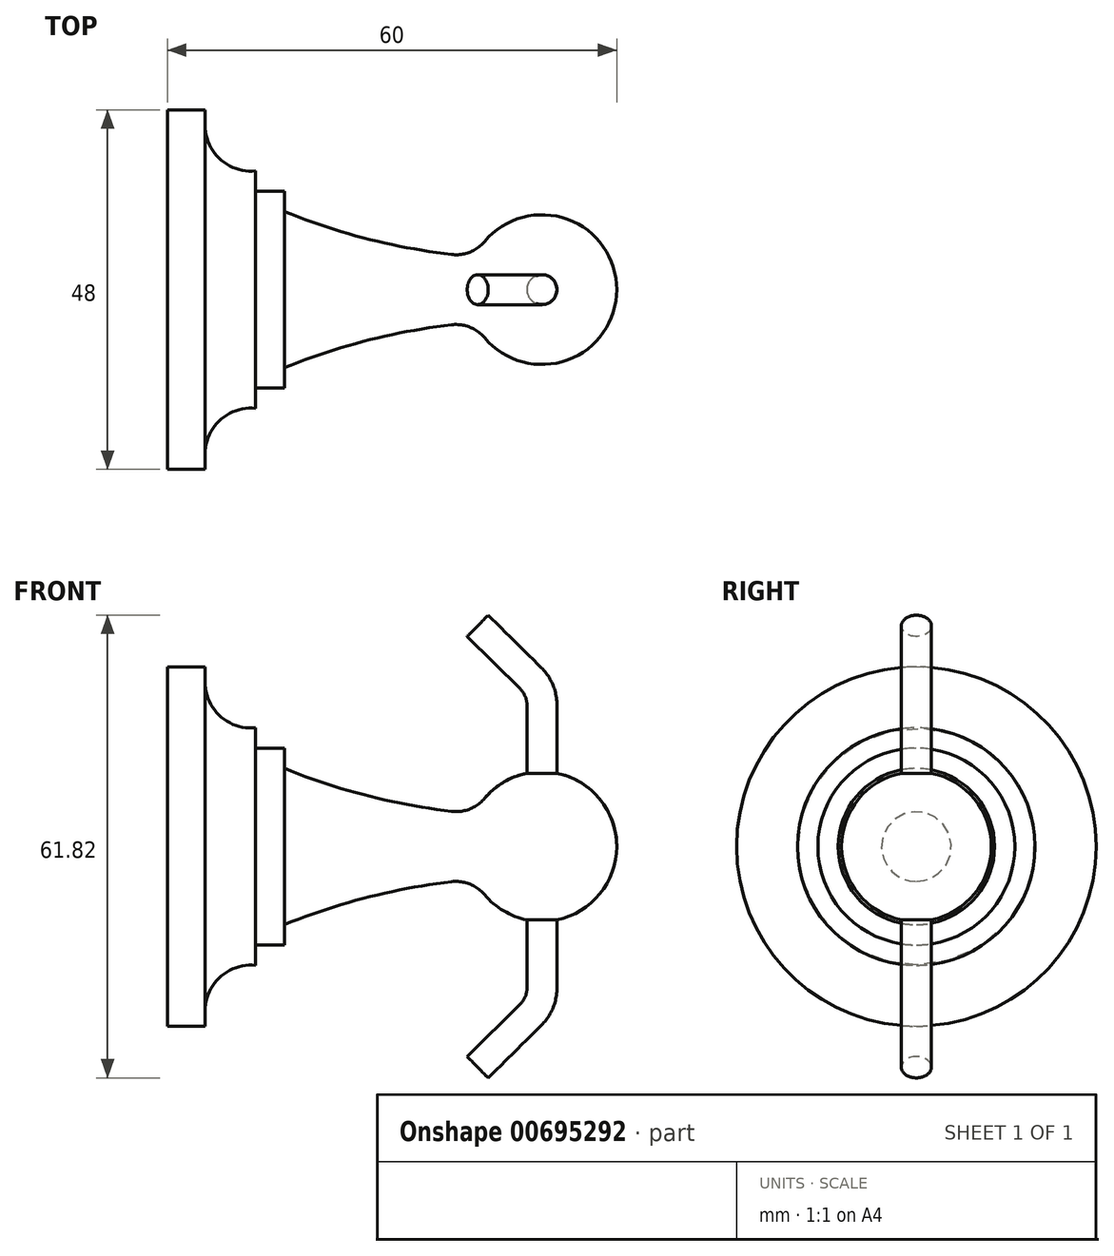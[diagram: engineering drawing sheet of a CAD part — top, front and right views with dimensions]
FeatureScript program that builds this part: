
annotation { "Feature Type Name" : "Feature", "Feature Type Description" : "" }
export const myFeature = defineFeature(function(context is Context, id is Id, definition is map)
    precondition{}
    {
        {
            var Q0;
            Q0=qCreatedBy(makeId("Front.planeOp"),FACE);
            var sketch = newSketch(context, id + "F0", { "sketchPlane" : qUnion([Q0])});
            skLineSegment(sketch, "E0", {"start": v(0, 0) * mm, "end": v(-60, 0) * mm});
            skArc(sketch, "E1", {"start": v(0, 0) * mm, "mid": v(-7.75, 9.74) * mm, "end": v(-18.99, 4.38) * mm});
            skLineSegment(sketch, "E2", {"start": v(-60, 0) * mm, "end": v(-60, 24) * mm});
            skLineSegment(sketch, "E3", {"start": v(-60, 24) * mm, "end": v(-55, 24) * mm});
            skLineSegment(sketch, "E4", {"start": v(-55, 24) * mm, "end": v(-55, 22) * mm});
            skArc(sketch, "E5", {"start": v(-55, 22) * mm, "mid": v(-52.97, 17.43) * mm, "end": v(-48.22, 15.86) * mm});
            skArc(sketch, "E6", {"start": v(-44.4, 10.44) * mm, "mid": v(-31.92, 6.45) * mm, "end": v(-18.99, 4.38) * mm});
            skLineSegment(sketch, "E7", {"start": v(-48.22, 15.86) * mm, "end": v(-48.22, 13.15) * mm});
            skLineSegment(sketch, "E8", {"start": v(-48.22, 13.15) * mm, "end": v(-44.4, 13.15) * mm});
            skLineSegment(sketch, "E9", {"start": v(-44.4, 13.15) * mm, "end": v(-44.4, 10.44) * mm});
            skSolve(sketch);
        }
        {
            var Q0;
            Q0 = qSketchRegion(id + "F0", true);
            var Q1;
            Q1=sQuery(id+"F0.wireOp",EDGE,"E0");
            revolve(context, id + "F1", {"entities" : qUnion([Q0]), "axis" : qUnion([Q1]), "revolveType" : RevolveType.FULL});
        }
        {
            var Q0;
            Q0=makeQuery(id+"F1.opRevolve","SWEPT_EDGE",EDGE,{"disambiguationData":[OSD([sQuery(id+"F0.wireOp",EDGE,"E1"),sQuery(id+"F0.wireOp",EDGE,"E6")])]});
            fillet(context, id + "F2", {"entities" : qUnion([Q0]), "radius" : 5 * mm, "tangentPropagation" : true, "allowEdgeOverflow" : false});
        }
        {
            var Q0;
            Q0=qCreatedBy(makeId("Top.planeOp"),FACE);
            var sketch = newSketch(context, id + "F3", { "sketchPlane" : qUnion([Q0])});
            skCircle(sketch, "E10", {"center": v(-10, 0) * mm, "radius": 2 * mm});
            skSolve(sketch);
        }
        {
            var Q0;
            Q0 = qSketchRegion(id + "F3", true);
            extrude(context, id + "F4", {"entities" : qUnion([Q0]), "operationType" : NewBodyOperationType.REMOVE, "oppositeDirection" : true, "depth" : 25 * mm, "offsetDistance" : 25 * mm, "hasSecondDirection" : true, "secondDirectionOppositeDirection" : false, "secondDirectionDepth" : 25 * mm});
        }
        {
            var Q0;
            Q0=qCreatedBy(makeId("Front.planeOp"),FACE);
            var sketch = newSketch(context, id + "F5", { "sketchPlane" : qUnion([Q0])});
            skLineSegment(sketch, "E11", {"start": v(-10, 0) * mm, "end": v(-10, -18.91) * mm});
            skLineSegment(sketch, "E12", {"start": v(-11.48, -22.47) * mm, "end": v(-18.57, -29.5) * mm});
            skPoint(sketch, "E13.visualSharp", {"position": v(-10, -21) * mm});
            skArc(sketch, "E13.filletArc", {"start": v(-11.48, -22.47) * mm, "mid": v(-10.39, -20.84) * mm, "end": v(-10, -18.91) * mm});
            skSolve(sketch);
        }
        {
            var Q0;
            Q0=qCreatedBy(makeId("Top.planeOp"),FACE);
            var sketch = newSketch(context, id + "F6", { "sketchPlane" : qUnion([Q0])});
            skCircle(sketch, "E14", {"center": v(-10, 0) * mm, "radius": 2 * mm});
            skSolve(sketch);
        }
        {
            var Q0;
            Q0=makeQuery(id+"F6.imprint","IMPRINT",FACE,{"disambiguationData":[TD([[makeQuery(id+"F6.imprint","IMPRINT",EDGE,{"derivedFrom":sQuery(id+"F6.wireOp",EDGE,"E14")}),1.0]])]});
            var Q1;
            Q1=sQuery(id+"F5.wireOp",EDGE,"E11");
            var Q2;
            Q2=sQuery(id+"F5.wireOp",EDGE,"E13.filletArc");
            var Q3;
            Q3=sQuery(id+"F5.wireOp",EDGE,"E12");
            sweep(context, id + "F7", {"operationType" : NewBodyOperationType.ADD, "profiles" : qUnion([Q0]), "path" : qUnion([Q1, Q2, Q3])});
        }
        {
            var Q0;
            Q0=makeQuery(id+"F1.opRevolve","SWEPT_BODY",BODY,{"disambiguationData":[OSD([sQuery(id+"F0.wireOp",EDGE,"E0"),sQuery(id+"F0.wireOp",EDGE,"E1"),sQuery(id+"F0.wireOp",EDGE,"E2"),sQuery(id+"F0.wireOp",EDGE,"E3"),sQuery(id+"F0.wireOp",EDGE,"E4"),sQuery(id+"F0.wireOp",EDGE,"E5"),sQuery(id+"F0.wireOp",EDGE,"E6"),sQuery(id+"F0.wireOp",EDGE,"E7"),sQuery(id+"F0.wireOp",EDGE,"E8"),sQuery(id+"F0.wireOp",EDGE,"E9")])]});
            var Q1;
            Q1=qCreatedBy(makeId("Top.planeOp"),FACE);
            mirror(context, id + "F8", {"operationType" : NewBodyOperationType.ADD, "entities" : qUnion([Q0]), "mirrorPlane" : qUnion([Q1])});
        }
    });
